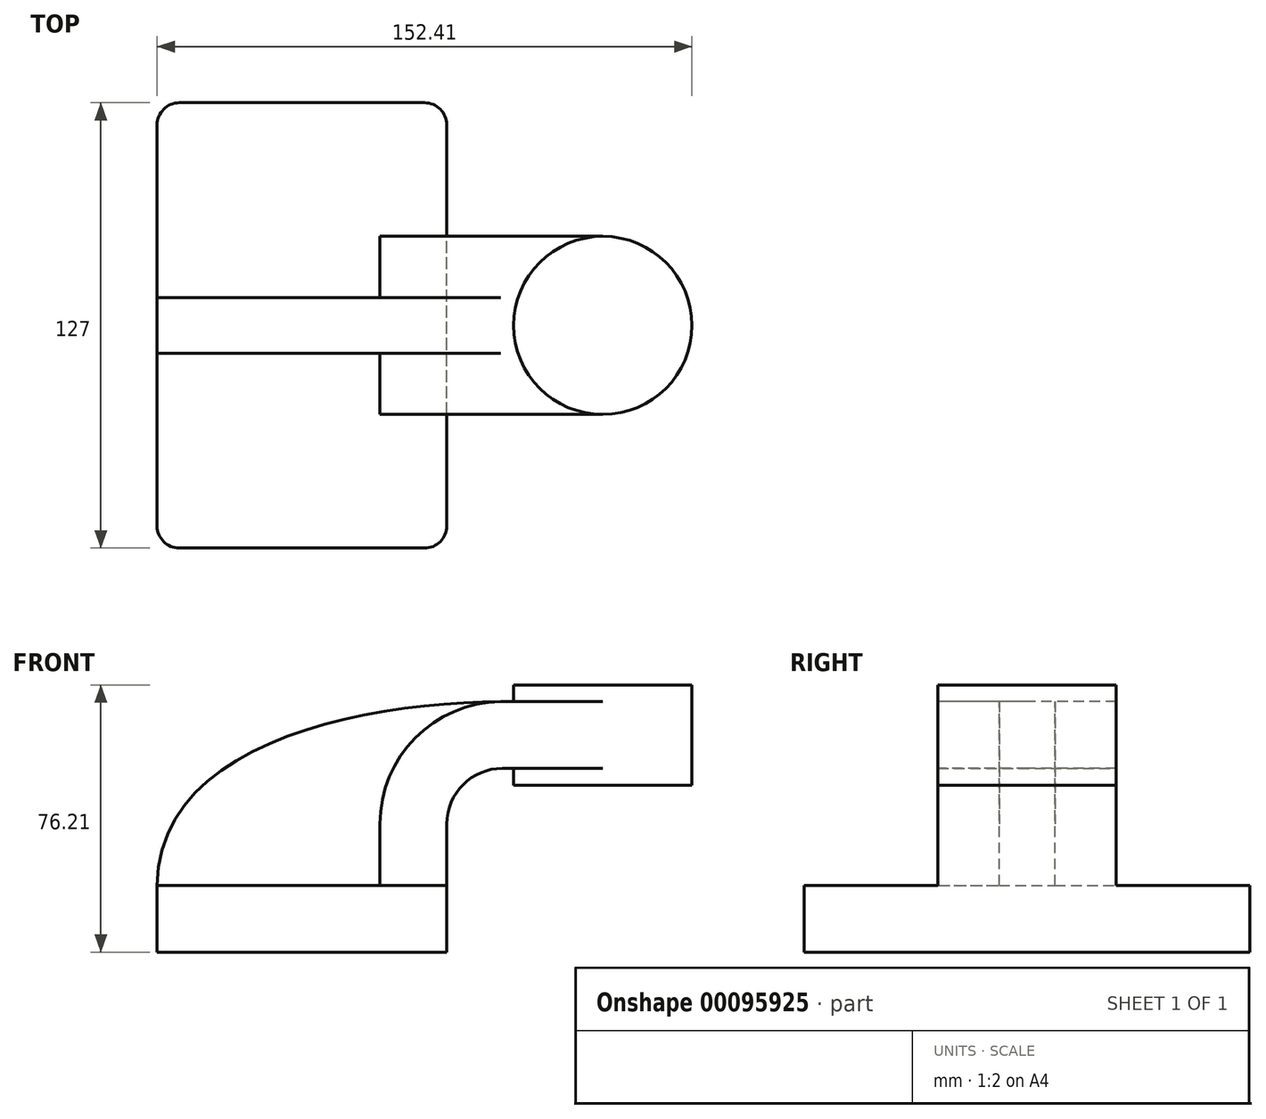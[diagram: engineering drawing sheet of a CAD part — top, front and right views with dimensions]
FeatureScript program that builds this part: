
annotation { "Feature Type Name" : "Feature", "Feature Type Description" : "" }
export const myFeature = defineFeature(function(context is Context, id is Id, definition is map)
    precondition{}
    {
        {
            var Q0;
            Q0=qCreatedBy(makeId("Front.planeOp"),FACE);
            var sketch = newSketch(context, id + "F0", { "sketchPlane" : qUnion([Q0])});
            skLineSegment(sketch, "E0.bottom", {"start": v(41.28, -9.52) * mm, "end": v(-41.28, -9.53) * mm});
            skLineSegment(sketch, "E0.top", {"start": v(41.28, 9.53) * mm, "end": v(-41.28, 9.52) * mm});
            skLineSegment(sketch, "E0.left", {"start": v(41.28, -9.53) * mm, "end": v(41.28, 9.53) * mm});
            skLineSegment(sketch, "E0.right", {"start": v(-41.28, -9.53) * mm, "end": v(-41.28, 9.52) * mm});
            skPoint(sketch, "E0.middle", {"position": v(0, 0) * mm});
            skLineSegment(sketch, "E1.bottom", {"start": v(111.12, 38.1) * mm, "end": v(60.32, 38.1) * mm});
            skLineSegment(sketch, "E1.top", {"start": v(111.12, 66.67) * mm, "end": v(60.32, 66.67) * mm});
            skLineSegment(sketch, "E1.left", {"start": v(111.12, 38.1) * mm, "end": v(111.12, 66.67) * mm});
            skLineSegment(sketch, "E1.right", {"start": v(60.32, 38.1) * mm, "end": v(60.32, 66.67) * mm});
            skPoint(sketch, "E1.middle", {"position": v(85.72, 52.39) * mm});
            skLineSegment(sketch, "E2", {"start": v(41.27, 9.53) * mm, "end": v(41.27, 27) * mm});
            skArc(sketch, "E3", {"start": v(41.27, 27) * mm, "mid": v(45.92, 38.23) * mm, "end": v(57.15, 42.88) * mm});
            skLineSegment(sketch, "E4", {"start": v(57.15, 42.88) * mm, "end": v(85.72, 42.88) * mm});
            skLineSegment(sketch, "E5.0", {"start": v(57.15, 61.93) * mm, "end": v(85.73, 61.93) * mm});
            skArc(sketch, "E5.1", {"start": v(22.22, 27) * mm, "mid": v(32.45, 51.7) * mm, "end": v(57.15, 61.93) * mm});
            skLineSegment(sketch, "E5.2", {"start": v(22.22, 9.53) * mm, "end": v(22.22, 27) * mm});
            skLineSegment(sketch, "E6", {"start": v(85.72, 42.88) * mm, "end": v(85.72, 66.67) * mm});
            skLineSegment(sketch, "E7", {"start": v(85.72, 38.1) * mm, "end": v(85.72, 66.67) * mm});
            skFitSpline(sketch, "E8", {"points": [v(-41.28, 9.53) * mm, v(57.15, 61.93) * mm], "startDerivative": vector(1.5, 123.4) * mm, "endDerivative": vector(117.62, 0.68) * mm});
            skSolve(sketch);
        }
        {
            var Q0;
            Q0=makeQuery(id+"F0.imprint","IMPRINT",FACE,{"disambiguationData":[TD([[makeQuery(id+"F0.imprint","IMPRINT",EDGE,{"derivedFrom":sQuery(id+"F0.wireOp",EDGE,"E0.bottom")}),-1.0]])]});
            extrude(context, id + "F1", {"entities" : qUnion([Q0]), "endBound" : BoundingType.SYMMETRIC, "depth" : 127 * mm});
        }
        {
            var Q0;
            {var subQ1=sQuery(id+"F0.wireOp",EDGE,"E2");Q0=makeQuery(id+"F0.imprint","IMPRINT",FACE,{"disambiguationData":[TD([[makeQuery(id+"F0.imprint","IMPRINT",EDGE,{"derivedFrom":subQ1}),1.0]])]});}
            var Q1;
            {var subQ0=sQuery(id+"F0.wireOp",EDGE,"E4");var subQ1=sQuery(id+"F0.wireOp",EDGE,"E1.right");var subQ2=makeQuery(id+"F0.imprint","INTERSECT",VERTEX,{"derivedFrom":[subQ1,subQ0]});Q1=makeQuery(id+"F0.imprint","IMPRINT",FACE,{"disambiguationData":[TD([[makeQuery(id+"F0.imprint","IMPRINT",EDGE,{"disambiguationData":[TD([[subQ2,-1.0]])],"derivedFrom":subQ1}),-1.0]])]});}
            extrude(context, id + "F2", {"entities" : qUnion([Q0, Q1]), "operationType" : NewBodyOperationType.ADD, "endBound" : BoundingType.SYMMETRIC, "depth" : 50.8 * mm});
        }
        {
            var Q0;
            {var subQ3=sQuery(id+"F0.wireOp",EDGE,"E5.2");Q0=makeQuery(id+"F0.imprint","IMPRINT",FACE,{"disambiguationData":[TD([[makeQuery(id+"F0.imprint","IMPRINT",EDGE,{"derivedFrom":subQ3}),1.0]])]});}
            extrude(context, id + "F3", {"entities" : qUnion([Q0]), "operationType" : NewBodyOperationType.ADD, "endBound" : BoundingType.SYMMETRIC, "depth" : 15.88 * mm});
        }
        {
            var Q0;
            {var subQ4=sQuery(id+"F0.wireOp",EDGE,"E1.left");Q0=makeQuery(id+"F0.imprint","IMPRINT",FACE,{"disambiguationData":[TD([[makeQuery(id+"F0.imprint","IMPRINT",EDGE,{"derivedFrom":subQ4}),1.0]])]});}
            var Q1;
            Q1=sQuery(id+"F0.wireOp",EDGE,"E7");
            revolve(context, id + "F4", {"operationType" : NewBodyOperationType.ADD, "entities" : qUnion([Q0]), "axis" : qUnion([Q1]), "revolveType" : RevolveType.FULL});
        }
        {
            var Q0;
            Q0=makeQuery(id+"F1.opExtrude","CAP_EDGE",EDGE,{"disambiguationData":[OSD([sQuery(id+"F0.wireOp",EDGE,"E0.left")])],"isStart":false});
            var Q1;
            Q1=makeQuery(id+"F1.opExtrude","CAP_EDGE",EDGE,{"disambiguationData":[OSD([sQuery(id+"F0.wireOp",EDGE,"E0.right")])],"isStart":false});
            var Q2;
            Q2=makeQuery(id+"F1.opExtrude","CAP_EDGE",EDGE,{"disambiguationData":[OSD([sQuery(id+"F0.wireOp",EDGE,"E0.left")])],"isStart":true});
            var Q3;
            Q3=makeQuery(id+"F1.opExtrude","CAP_EDGE",EDGE,{"disambiguationData":[OSD([sQuery(id+"F0.wireOp",EDGE,"E0.right")])],"isStart":true});
            fillet(context, id + "F5", {"entities" : qUnion([Q0, Q1, Q2, Q3]), "radius" : 6.35 * mm, "tangentPropagation" : true, "allowEdgeOverflow" : false});
        }
    });
